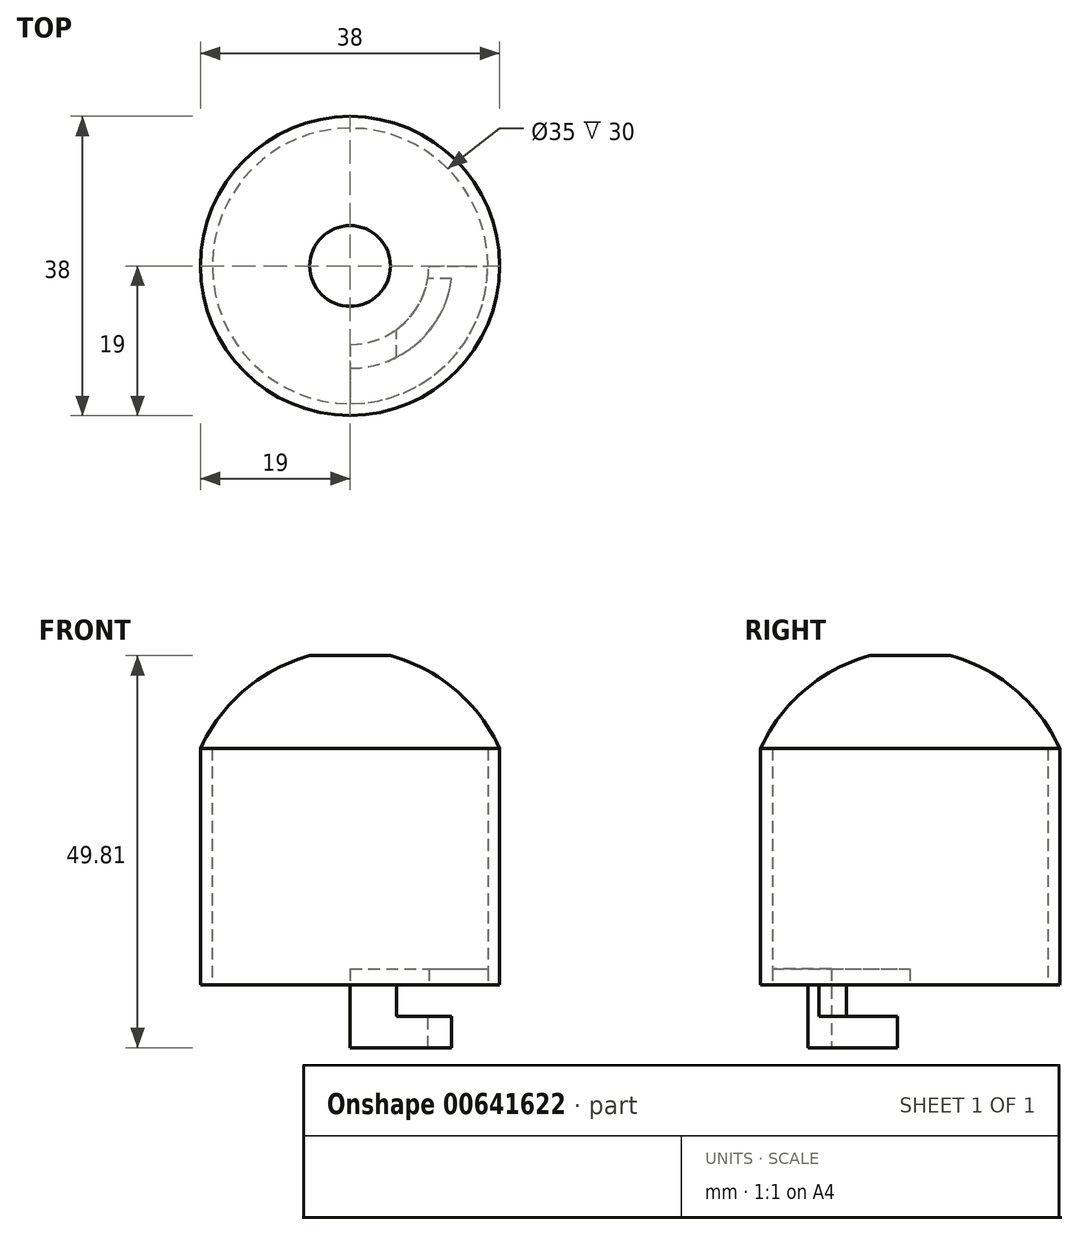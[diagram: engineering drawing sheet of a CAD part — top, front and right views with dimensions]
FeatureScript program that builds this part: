
annotation { "Feature Type Name" : "Feature", "Feature Type Description" : "" }
export const myFeature = defineFeature(function(context is Context, id is Id, definition is map)
    precondition{}
    {
        {
            var Q0;
            Q0=qCreatedBy(makeId("Top.planeOp"),FACE);
            var sketch = newSketch(context, id + "F0", { "sketchPlane" : qUnion([Q0])});
            skCircle(sketch, "E0", {"center": v(0, 0) * mm, "radius": 19 * mm});
            skCircle(sketch, "E1", {"center": v(0, 0) * mm, "radius": 17.5 * mm});
            skSolve(sketch);
        }
        {
            var Q0;
            Q0 = qSketchRegion(id + "F0", true);
            extrude(context, id + "F1", {"entities" : qUnion([Q0]), "depth" : 30 * mm, "offsetDistance" : 25 * mm});
        }
        {
            var Q0;
            Q0=qCreatedBy(makeId("Front.planeOp"),FACE);
            var sketch = newSketch(context, id + "F2", { "sketchPlane" : qUnion([Q0])});
            skLineSegment(sketch, "E2", {"start": v(0, 30) * mm, "end": v(-20, 30) * mm});
            skLineSegment(sketch, "E3", {"start": v(-20, 30) * mm, "end": v(19, 30) * mm});
            skLineSegment(sketch, "E4", {"start": v(0, 0) * mm, "end": v(0, 30) * mm});
            skLineSegment(sketch, "E5", {"start": v(-20, 30) * mm, "end": v(-20, 0) * mm});
            skArc(sketch, "E6", {"start": v(19, 30) * mm, "mid": v(13.38, 37.45) * mm, "end": v(5.13, 41.8) * mm});
            skLineSegment(sketch, "E7", {"start": v(0, 30) * mm, "end": v(0, 41.8) * mm});
            skLineSegment(sketch, "E8", {"start": v(0, 41.8) * mm, "end": v(5.13, 41.8) * mm});
            skSolve(sketch);
        }
        {
            var Q0;
            {var subQ0=sQuery(id+"F2.wireOp",EDGE,"E6");Q0=makeQuery(id+"F2.imprint","IMPRINT",FACE,{"disambiguationData":[TD([[makeQuery(id+"F2.imprint","IMPRINT",EDGE,{"derivedFrom":subQ0}),1.0]])]});}
            var Q1;
            Q1=sQuery(id+"F2.wireOp",EDGE,"E7");
            revolve(context, id + "F3", {"operationType" : NewBodyOperationType.ADD, "entities" : qUnion([Q0]), "axis" : qUnion([Q1]), "revolveType" : RevolveType.FULL});
        }
        {
            var Q0;
            Q0=qCreatedBy(makeId("Top.planeOp"),FACE);
            var sketch = newSketch(context, id + "F4", { "sketchPlane" : qUnion([Q0])});
            skPoint(sketch, "E9.endSnap0", {"position": v(0.75, -9.25) * mm});
            skLineSegment(sketch, "E10", {"start": v(0, -10) * mm, "end": v(0, -19) * mm});
            skLineSegment(sketch, "E11", {"start": v(0, -19) * mm, "end": v(0, -10) * mm});
            skArc(sketch, "E12", {"start": v(0, -19) * mm, "mid": v(13.42, -13.43) * mm, "end": v(18.97, 0) * mm});
            skLineSegment(sketch, "E13", {"start": v(10, 0) * mm, "end": v(18.97, 0) * mm});
            skArc(sketch, "E14", {"start": v(10, 0) * mm, "mid": v(7.07, -7.07) * mm, "end": v(0, -10) * mm});
            skSolve(sketch);
        }
        {
            var Q0;
            {var subQ0=sQuery(id+"F4.wireOp",EDGE,"uPRqpHzI-vHT0-QglQ-HLLu-WeeHTGpD93Ii");Q0=makeQuery(id+"F4.imprint","IMPRINT",FACE,{"disambiguationData":[TD([[makeQuery(id+"F4.imprint","IMPRINT",EDGE,{"derivedFrom":subQ0}),1.0]])]});}
            var Q1;
            {var subQ0=sQuery(id+"F4.wireOp",EDGE,"E12");Q1=makeQuery(id+"F4.imprint","IMPRINT",FACE,{"disambiguationData":[TD([[makeQuery(id+"F4.imprint","IMPRINT",EDGE,{"derivedFrom":subQ0}),1.0]])]});}
            extrude(context, id + "F5", {"entities" : qUnion([Q0, Q1]), "operationType" : NewBodyOperationType.ADD, "depth" : 2 * mm, "offsetDistance" : 25 * mm});
        }
        {
            var Q0;
            Q0=makeQuery(id+"F5.boolean.opBoolean","MERGE",FACE,{"derivedFrom":[makeQuery(id+"F1.opExtrude","CAP_FACE",FACE,{"disambiguationData":[OSD([sQuery(id+"F0.wireOp",EDGE,"E0"),sQuery(id+"F0.wireOp",EDGE,"E1")])],"isStart":true}),makeQuery(id+"F5.opExtrude","CAP_FACE",FACE,{"disambiguationData":[OSD([sQuery(id+"F4.wireOp",EDGE,"E9"),sQuery(id+"F4.wireOp",EDGE,"uPRqpHzI-vHT0-QglQ-HLLu-WeeHTGpD93Ii")])],"isStart":true})]});
            var sketch = newSketch(context, id + "F6", { "sketchPlane" : qUnion([Q0])});
            skArc(sketch, "E15", {"start": v(12.9, 1.61) * mm, "mid": v(8.6, 9.75) * mm, "end": v(0, 13) * mm});
            skArc(sketch, "E16.0", {"start": v(9.87, 1.61) * mm, "mid": v(6.48, 7.62) * mm, "end": v(0, 10) * mm});
            skLineSegment(sketch, "E17", {"start": v(0, 13) * mm, "end": v(0, 10) * mm});
            skLineSegment(sketch, "E18", {"start": v(9.87, 1.61) * mm, "end": v(12.9, 1.61) * mm});
            skSolve(sketch);
        }
        {
            var Q0;
            Q0 = qSketchRegion(id + "F6", true);
            extrude(context, id + "F7", {"entities" : qUnion([Q0]), "operationType" : NewBodyOperationType.ADD, "depth" : 8 * mm, "offsetDistance" : 25 * mm});
        }
        {
            var Q0;
            Q0=makeQuery(id+"F7.opExtrude","SWEPT_FACE",FACE,{"disambiguationData":[OSD([sQuery(id+"F6.wireOp",EDGE,"E18")])]});
            var sketch = newSketch(context, id + "F8", { "sketchPlane" : qUnion([Q0])});
            skLineSegment(sketch, "E19", {"start": v(-5.9, 0) * mm, "end": v(-12.9, 0) * mm});
            skLineSegment(sketch, "E20", {"start": v(-12.9, 0) * mm, "end": v(-12.9, -4) * mm});
            skLineSegment(sketch, "E21", {"start": v(-12.9, -4) * mm, "end": v(-5.9, -4) * mm});
            skLineSegment(sketch, "E22", {"start": v(-5.9, -4) * mm, "end": v(-5.9, 0) * mm});
            skSolve(sketch);
        }
        {
            var Q0;
            {var subQ0=sQuery(id+"F8.wireOp",EDGE,"E20");Q0=makeQuery(id+"F8.imprint","IMPRINT",FACE,{"disambiguationData":[TD([[makeQuery(id+"F8.imprint","IMPRINT",EDGE,{"derivedFrom":subQ0}),-1.0]])]});}
            var Q1;
            {var subQ3=sQuery(id+"F8.wireOp",EDGE,"E22");Q1=makeQuery(id+"F8.imprint","IMPRINT",FACE,{"disambiguationData":[TD([[makeQuery(id+"F8.imprint","IMPRINT",EDGE,{"derivedFrom":subQ3}),1.0]])]});}
            extrude(context, id + "F9", {"entities" : qUnion([Q0, Q1]), "operationType" : NewBodyOperationType.REMOVE, "oppositeDirection" : true, "depth" : 25 * mm, "offsetDistance" : 25 * mm});
        }
    });
